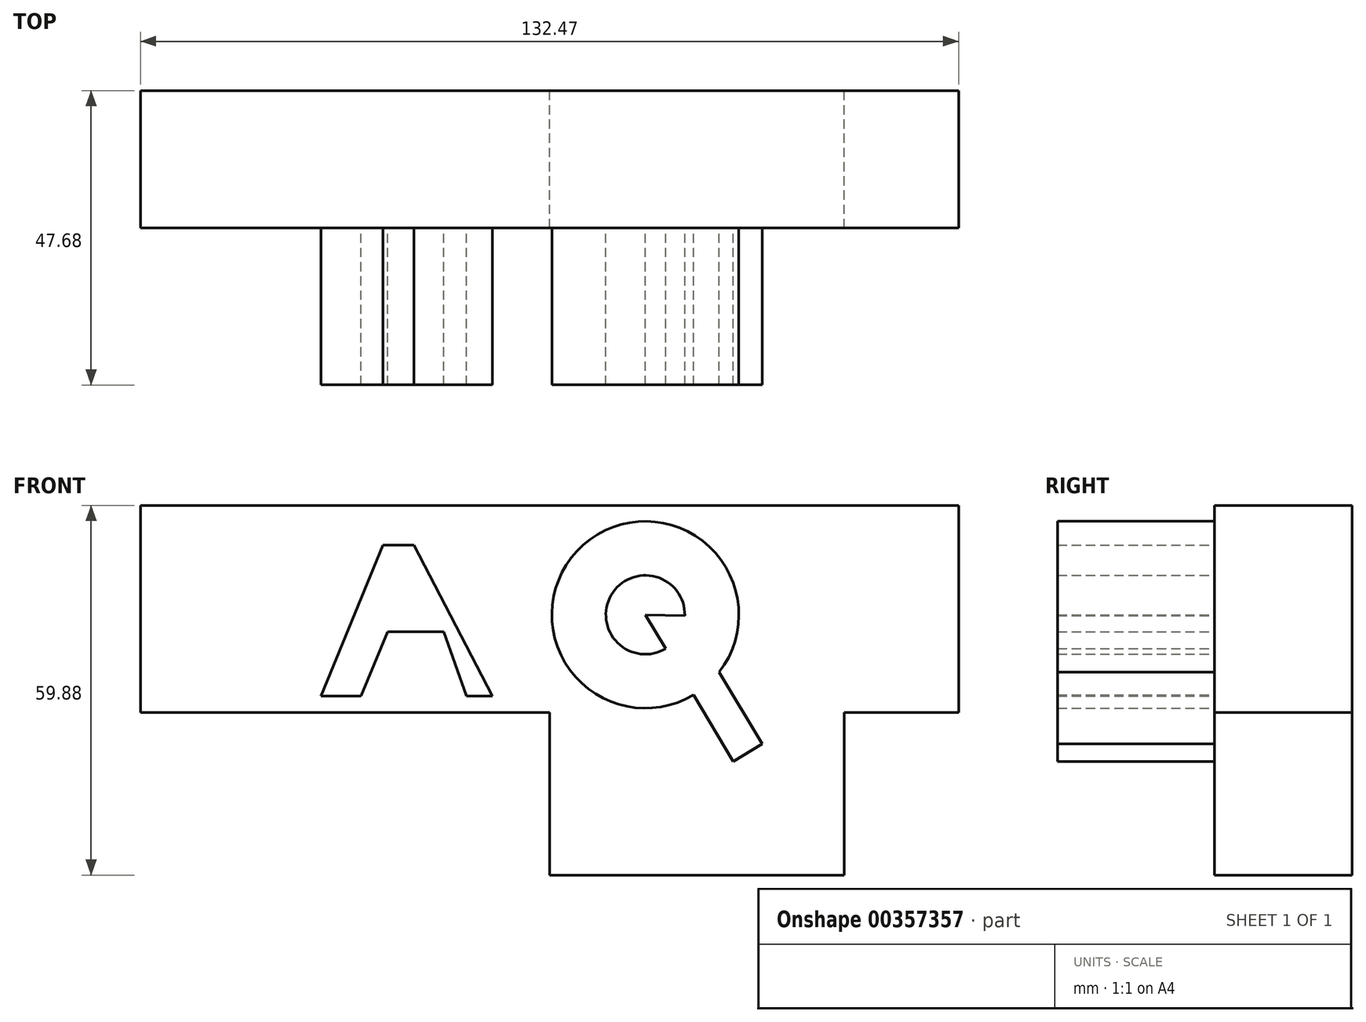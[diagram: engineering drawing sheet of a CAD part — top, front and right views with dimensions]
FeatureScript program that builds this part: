
annotation { "Feature Type Name" : "Feature", "Feature Type Description" : "" }
export const myFeature = defineFeature(function(context is Context, id is Id, definition is map)
    precondition{}
    {
        {
            var Q0;
            Q0=qCreatedBy(makeId("Front.planeOp"),FACE);
            var sketch = newSketch(context, id + "F0", { "sketchPlane" : qUnion([Q0])});
            skLineSegment(sketch, "E0.bottom", {"start": v(0, 0) * mm, "end": v(-66.23, 0) * mm});
            skLineSegment(sketch, "E0.top", {"start": v(0, 33.55) * mm, "end": v(-66.23, 33.55) * mm});
            skLineSegment(sketch, "E0.left", {"start": v(0, 0) * mm, "end": v(0, 33.55) * mm});
            skLineSegment(sketch, "E0.right", {"start": v(-66.23, 0) * mm, "end": v(-66.23, 33.55) * mm});
            skLineSegment(sketch, "E1.bottom", {"start": v(-47.73, 0) * mm, "end": v(0, 0) * mm});
            skLineSegment(sketch, "E1.top", {"start": v(-47.73, -26.33) * mm, "end": v(0, -26.33) * mm});
            skLineSegment(sketch, "E1.left", {"start": v(-47.73, 0) * mm, "end": v(-47.73, -26.33) * mm});
            skLineSegment(sketch, "E1.right", {"start": v(0, 0) * mm, "end": v(0, -26.33) * mm});
            skLineSegment(sketch, "E2.bottom", {"start": v(0, -26.33) * mm, "end": v(47.73, -26.33) * mm});
            skLineSegment(sketch, "E2.top", {"start": v(0, 0) * mm, "end": v(47.73, 0) * mm});
            skLineSegment(sketch, "E2.left", {"start": v(0, -26.33) * mm, "end": v(0, 0) * mm});
            skLineSegment(sketch, "E2.right", {"start": v(47.73, -26.33) * mm, "end": v(47.73, 0) * mm});
            skLineSegment(sketch, "E3.bottom", {"start": v(0, 33.55) * mm, "end": v(66.24, 33.55) * mm});
            skLineSegment(sketch, "E3.top", {"start": v(0, 0) * mm, "end": v(66.24, 0) * mm});
            skLineSegment(sketch, "E3.left", {"start": v(0, 33.55) * mm, "end": v(0, 0) * mm});
            skLineSegment(sketch, "E3.right", {"start": v(66.24, 33.55) * mm, "end": v(66.24, 0) * mm});
            skPoint(sketch, "E4.oppositeSnap0", {"position": v(23.86, -26.33) * mm});
            skLineSegment(sketch, "E4.bottom", {"start": v(-23.86, -26.33) * mm, "end": v(23.86, -26.33) * mm});
            skSolve(sketch);
        }
        {
            var Q0;
            Q0=makeQuery(id+"F0.imprint","IMPRINT",FACE,{"disambiguationData":[TD([[makeQuery(id+"F0.imprint","IMPRINT",EDGE,{"derivedFrom":sQuery(id+"F0.wireOp",EDGE,"E0.bottom")}),-1.0]])]});
            var Q1;
            {var subQ3=sQuery(id+"F0.wireOp",EDGE,"E2.bottom");Q1=makeQuery(id+"F0.imprint","IMPRINT",FACE,{"disambiguationData":[TD([[makeQuery(id+"F0.imprint","IMPRINT",EDGE,{"derivedFrom":subQ3}),1.0]])]});}
            var Q2;
            Q2=makeQuery(id+"F0.imprint","IMPRINT",FACE,{"disambiguationData":[TD([[makeQuery(id+"F0.imprint","IMPRINT",EDGE,{"derivedFrom":sQuery(id+"F0.wireOp",EDGE,"E3.bottom")}),-1.0]])]});
            var Q3;
            Q3=makeQuery(id+"F0.imprint","IMPRINT",FACE,{"disambiguationData":[TD([[makeQuery(id+"F0.imprint","IMPRINT",EDGE,{"derivedFrom":sQuery(id+"F0.wireOp",EDGE,"E4.top")}),1.0]])]});
            var Q4;
            Q4=makeQuery(id+"F0.imprint","IMPRINT",FACE,{"disambiguationData":[TD([[makeQuery(id+"F0.imprint","IMPRINT",EDGE,{"derivedFrom":sQuery(id+"F0.wireOp",EDGE,"E1.bottom")}),-1.0]])]});
            extrude(context, id + "F1", {"entities" : qUnion([Q0, Q1, Q2, Q3, Q4]), "endBound" : BoundingType.SYMMETRIC, "depth" : 22.28 * mm});
        }
        {
            var Q0;
            Q0=makeQuery(id+"F1.opExtrude","CAP_FACE",FACE,{"disambiguationData":[OSD([sQuery(id+"F0.wireOp",EDGE,"E0.bottom"),sQuery(id+"F0.wireOp",EDGE,"E0.top"),sQuery(id+"F0.wireOp",EDGE,"E0.right"),sQuery(id+"F0.wireOp",EDGE,"E1.top"),sQuery(id+"F0.wireOp",EDGE,"E1.left"),sQuery(id+"F0.wireOp",EDGE,"E2.bottom"),sQuery(id+"F0.wireOp",EDGE,"E2.right"),sQuery(id+"F0.wireOp",EDGE,"E3.bottom"),sQuery(id+"F0.wireOp",EDGE,"E3.top"),sQuery(id+"F0.wireOp",EDGE,"E3.right"),sQuery(id+"F0.wireOp",EDGE,"E4.top"),sQuery(id+"F0.wireOp",EDGE,"E4.left"),sQuery(id+"F0.wireOp",EDGE,"E4.right")])],"isStart":false});
            var sketch = newSketch(context, id + "F2", { "sketchPlane" : qUnion([Q0])});
            skLineSegment(sketch, "E5", {"start": v(-26.96, 27.12) * mm, "end": v(-37, 2.65) * mm});
            skLineSegment(sketch, "E6", {"start": v(-37, 2.65) * mm, "end": v(-30.51, 2.65) * mm});
            skLineSegment(sketch, "E7", {"start": v(-30.51, 2.65) * mm, "end": v(-21.94, 23.56) * mm});
            skLineSegment(sketch, "E8", {"start": v(-21.94, 23.56) * mm, "end": v(-26.96, 27.12) * mm});
            skLineSegment(sketch, "E9", {"start": v(-26.22, 13.1) * mm, "end": v(-17.12, 13.1) * mm});
            skLineSegment(sketch, "E10", {"start": v(-17.12, 13.1) * mm, "end": v(-21.94, 23.56) * mm});
            skLineSegment(sketch, "E11", {"start": v(-17.12, 13.1) * mm, "end": v(-13.46, 2.65) * mm});
            skLineSegment(sketch, "E12", {"start": v(-13.46, 2.65) * mm, "end": v(-9.28, 2.65) * mm});
            skLineSegment(sketch, "E13", {"start": v(-9.28, 2.65) * mm, "end": v(-21.94, 27.12) * mm});
            skLineSegment(sketch, "E14", {"start": v(-21.94, 27.12) * mm, "end": v(-26.96, 27.12) * mm});
            skLineSegment(sketch, "E15", {"start": v(15.51, 15.83) * mm, "end": v(29.74, -7.92) * mm});
            skLineSegment(sketch, "E16", {"start": v(29.74, -7.92) * mm, "end": v(34.45, -5.1) * mm});
            skLineSegment(sketch, "E17", {"start": v(34.45, -5.1) * mm, "end": v(21.98, 15.71) * mm});
            skLineSegment(sketch, "E18", {"start": v(21.98, 15.71) * mm, "end": v(15.51, 15.83) * mm});
            skCircle(sketch, "E19", {"center": v(15.51, 15.83) * mm, "radius": 15.14 * mm});
            skCircle(sketch, "E20", {"center": v(15.51, 15.83) * mm, "radius": 6.39 * mm});
            skSolve(sketch);
        }
        {
            var Q0;
            Q0 = qSketchRegion(id + "F2", true);
            var Q1;
            {var subQ0=sQuery(id+"F2.wireOp",EDGE,"E16");Q1=makeQuery(id+"F2.imprint","IMPRINT",FACE,{"disambiguationData":[TD([[makeQuery(id+"F2.imprint","IMPRINT",EDGE,{"derivedFrom":subQ0}),1.0]])]});}
            var Q2;
            {var subQ1=sQuery(id+"F2.wireOp",EDGE,"E15");var subQ7=sQuery(id+"F2.wireOp",EDGE,"E20");var subQ9=makeQuery(id+"F2.imprint","INTERSECT",VERTEX,{"derivedFrom":[subQ1,subQ7]});Q2=makeQuery(id+"F2.imprint","IMPRINT",FACE,{"disambiguationData":[TD([[makeQuery(id+"F2.imprint","IMPRINT",EDGE,{"disambiguationData":[TD([[subQ9,-1.0]])],"derivedFrom":subQ1}),-1.0]])]});}
            var Q3;
            {var subQ0=sQuery(id+"F2.wireOp",EDGE,"E18");var subQ1=sQuery(id+"F2.wireOp",EDGE,"E15");var subQ2=makeQuery(id+"F2.imprint","INTERSECT",VERTEX,{"derivedFrom":[subQ1,subQ0]});Q3=makeQuery(id+"F2.imprint","IMPRINT",FACE,{"disambiguationData":[TD([[makeQuery(id+"F2.imprint","IMPRINT",EDGE,{"disambiguationData":[TD([[subQ2,-1.0]])],"derivedFrom":subQ1}),1.0]])]});}
            extrude(context, id + "F3", {"entities" : qUnion([Q0, Q1, Q2, Q3]), "operationType" : NewBodyOperationType.ADD, "depth" : 25.4 * mm});
        }
    });
